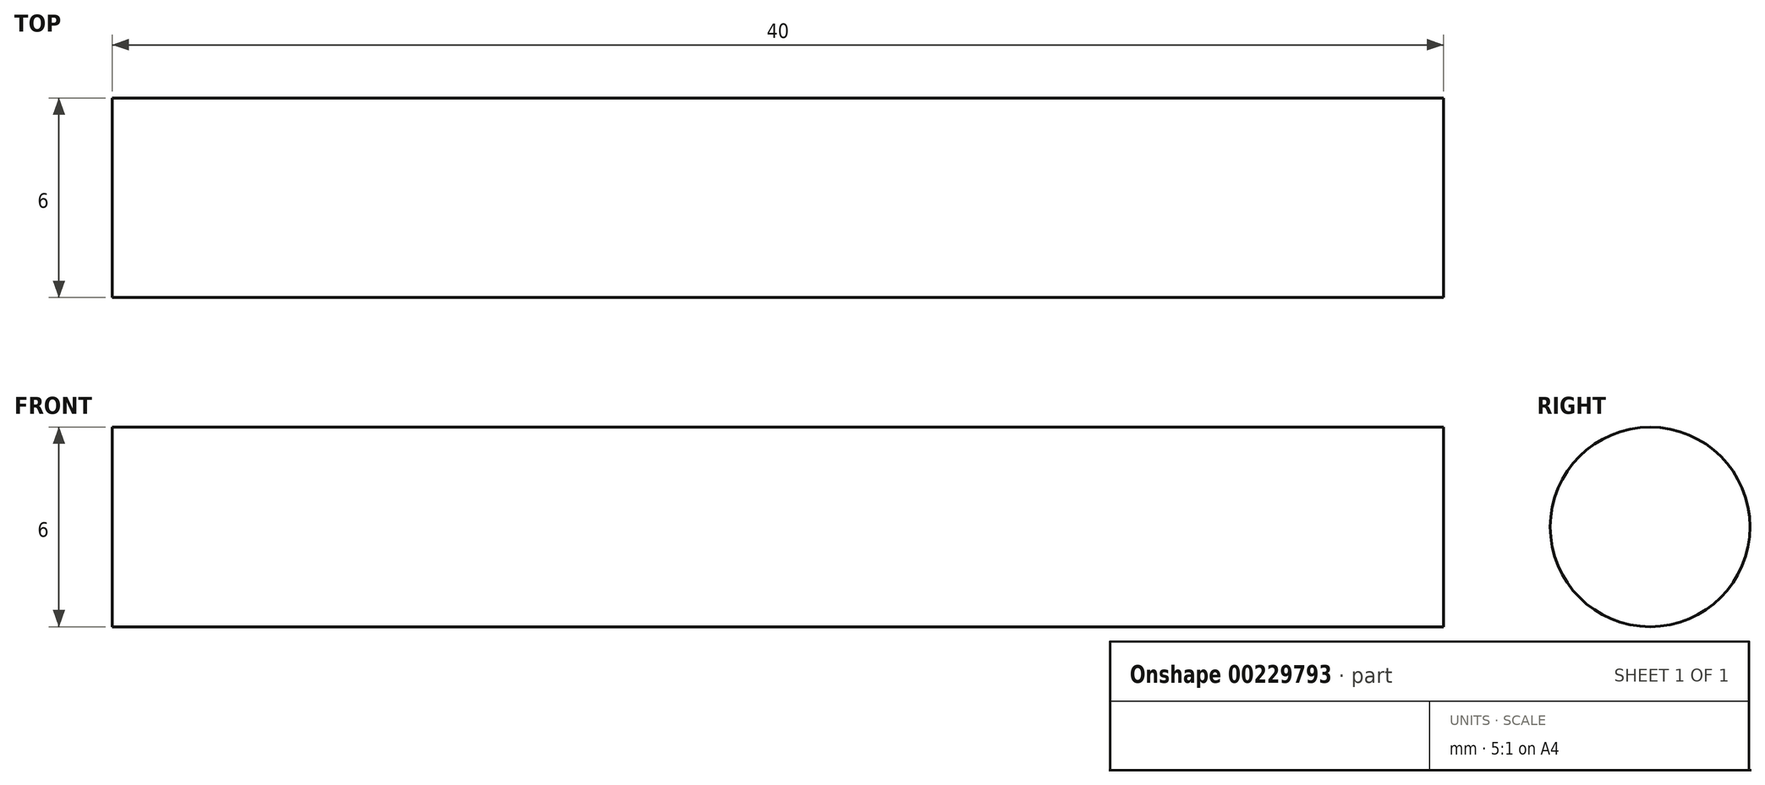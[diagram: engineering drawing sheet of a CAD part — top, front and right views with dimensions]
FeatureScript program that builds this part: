
annotation { "Feature Type Name" : "Feature", "Feature Type Description" : "" }
export const myFeature = defineFeature(function(context is Context, id is Id, definition is map)
    precondition{}
    {
        {
            var Q0;
            Q0=qCreatedBy(makeId("Front.planeOp"),FACE);
            var sketch = newSketch(context, id + "F0", { "sketchPlane" : qUnion([Q0])});
            skLineSegment(sketch, "E0", {"start": v(-20, 0) * mm, "end": v(-20, 3) * mm});
            skLineSegment(sketch, "E1", {"start": v(-20, 3) * mm, "end": v(0, 3) * mm});
            skLineSegment(sketch, "E2", {"start": v(-20, 0) * mm, "end": v(0, 0) * mm});
            skLineSegment(sketch, "E3.MirrorCS", {"start": v(20, 0) * mm, "end": v(20, 3) * mm});
            skLineSegment(sketch, "E4.MirrorCS", {"start": v(20, 3) * mm, "end": v(0, 3) * mm});
            skLineSegment(sketch, "E5.MirrorCS", {"start": v(20, 0) * mm, "end": v(0, 0) * mm});
            skSolve(sketch);
        }
        {
            var Q0;
            Q0=makeQuery(id+"F0.imprint","IMPRINT",FACE,{"disambiguationData":[TD([[makeQuery(id+"F0.imprint","IMPRINT",EDGE,{"derivedFrom":sQuery(id+"F0.wireOp",EDGE,"E0")}),-1.0]])]});
            var Q1;
            Q1=sQuery(id+"F0.wireOp",EDGE,"E5.MirrorCS");
            revolve(context, id + "F1", {"entities" : qUnion([Q0]), "axis" : qUnion([Q1]), "revolveType" : RevolveType.FULL});
        }
    });
